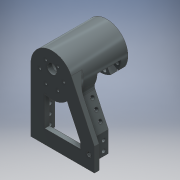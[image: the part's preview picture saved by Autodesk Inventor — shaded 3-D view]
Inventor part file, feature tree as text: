
AUTODESK INVENTOR PART (.ipt)
format: ipt  version: 2016 (Build 200138000, 138)  size: 401,920 bytes
history: native  units: mm
features: extrude x12, sketch x12, fillet x5, projected_geometry x3, plane x1
ambient origin geometry x8: Origin, YZ Plane, XZ Plane, XY Plane, X Axis, Y Axis, Z Axis, Center Point
bodies: Solid1 (feature_tree)
feature tree (33):
  extrude  "Extrusion1"  Depth=18.0mm
  extrude  "Extrusion23"  Depth=18.0mm
  extrude  "Extrusion24"  Depth=12.5mm
  extrude  "Extrusion27"  Depth=3.2mm
  extrude  "Extrusion28"  Depth=60.0mm TaperAngle=360.0deg
  extrude  "Extrusion29"  Depth=27.5mm
  extrude  "Extrusion30"  Depth=27.5mm
  extrude  "Extrusion31"  Depth=27.5mm
  extrude  "Extrusion32"  Depth=18.0mm
  plane  "Work Plane10"
  extrude  "Extrusion33"  Depth=82.5mm
  extrude  "Extrusion34"  Depth=46.0mm
  fillet  "Fillet10"  Radius=20.0mm
  fillet  "Fillet11"  Radius=37.5mm
  fillet  "Fillet12"  Radius=25.0mm
  fillet  "Fillet14"  Radius=18.75mm
  fillet  "Fillet15"  Radius=31.0mm
  extrude  "Extrusion35"  Depth=8.0mm
  sketch  "Sketch1"  dims[d7=18.0mm d9=18.0mm d10=18.0mm]
  sketch  "Sketch23"  dims[d11=18.0mm d12=18.0mm]
  sketch  "Sketch24"  dims[d13=82.5mm d14=12.5mm]
  sketch  "Sketch25"  dims[d15=7.0mm d16=3.2mm]
  sketch  "Sketch27"  dims[d17=15.5mm d18=60.0mm d20=360.0deg]
  projected_geometry  "Projected Loop1"
  sketch  "Sketch29"  dims[d22=30.0mm d23=27.5mm]
  sketch  "Sketch30"  dims[d24=18.0mm d25=27.5mm]
  projected_geometry  "Projected Loop2"
  sketch  "Sketch31"  dims[d26=27.5mm d27=27.5mm]
  sketch  "Sketch32"  dims[d29=18.0mm d30=18.0mm]
  sketch  "Sketch33"  dims[d31=82.5mm d32=82.5mm]
  projected_geometry  "Projected Loop3"
  sketch  "Sketch34"  dims[d33=6.0mm d34=0.0mm d107=46.0mm d178=20.0mm d179=0.0mm d180=37.5mm d181=25.0mm d182=0.0mm d183=18.75mm d188=31.0mm d189=0.0mm]
  sketch  "Sketch35"  dims[d190=9.0mm d191=0.0mm d199=2.3mm d200=2.3mm d201=2.3mm d202=2.3mm d203=2.3mm d204=2.3mm d205=2.3mm d206=16.0mm d207=0.0mm d208=25.0mm d209=0.0mm d210=5.0mm d211=5.0mm d212=6.0mm d213=6.0mm d214=6.0mm d215=12.0mm d216=5.0mm d217=0.0mm d218=5.0mm d219=5.0mm d220=5.0mm d221=6.0mm d222=12.0mm d223=12.0mm d224=5.0mm d225=0.0mm d226=5.0mm d227=5.0mm d228=5.0mm d229=5.0mm d230=6.0mm d231=6.0mm d232=12.0mm d233=12.0mm d234=12.0mm d235=5.0mm d236=0.0mm d237=10.4mm d238=5.0mm d239=0.0mm d240=8.0mm d241=8.0mm d242=8.0mm d244=8.0mm d245=8.0mm d246=0.0mm d247=0.0mm]
